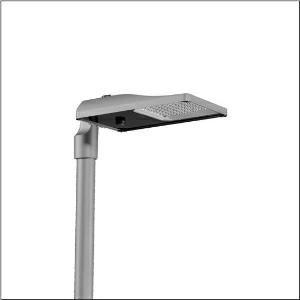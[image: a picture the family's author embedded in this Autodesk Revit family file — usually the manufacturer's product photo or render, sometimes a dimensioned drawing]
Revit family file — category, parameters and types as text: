
# Revit family: streetlight_sl_31_midi___st0_5a_5xh7b31t08ma_78a8
name_source: partatom
category: Lighting Fixtures
units: mm (PartAtom-declared; Revit-internal decimal feet)

## family parameters
Cut with Voids When Loaded = No
Host = Face
Light Source = No
Part Type = Normal
Room Calculation Point = No
Round Connector Dimension = Use Diameter
Shared = No

## types (1)
- --- (1 x LED, 19310 lm, 142.8 W, 3000K)
    Apparent Load = 143 VA
    CIE Flux Codes = 41 75 97 100 100
    Color Rendering = 70
    Color Temperature = 3000K
    Default Elevation = 1800 mm
    Description = Streetlight SL 31 midi, mast luminaire, primary light control with lens, of PMMA, primary optical cover: cover, of toughened safety glass, transparent, light distribution: ST0.5a, light emission: direct distribution, primary light characteristic: asymmetric, installation type: post-top, side-entry, LED, High Power LED, rated luminous flux: 19.310lm, luminous efficacy: 135lm/W, light colour: 730, colour temperature: 3000K, control: presetting dimming logarithmic, flexible luminous flux parameterisation, time-dependent luminous flux control, constant luminous flux control, power reduction, intelligent temperature release in ECG and LED module, overheat protection, with cable H07RN-F 2x 1.5mm², mains connection: 220..240V, AC, 50/60Hz, connection cable pre-assembled, cable length: 12,5m, start of lifetime: 143W, end of service life: 159W, reduction: 60W, luminaire housing, of diecast aluminium, powder-coated, Siteco® metallic grey (DB 702S), corrosivity category C5 high according to DIN EN ISO 12944, sealing non-destructively replaceable, multi-level sealing system, mast flange (76/60mm) included as standard, inclination: -15°..+20° (post-top) | -20°..+20° (side-entry), adjustable in 5° steps, no sealing on luminaire upper side, Smart Interface below and above, protection rating (complete): IP66, insulation class (complete): insulation class II (safety insulation), certification: CE, ENEC, ENEC+, VDE, UKCA, ZD4i, impact resistance: IK09, permissible operating ambient temperature for outdoor applications: -40..+50°C, standard-compliant lighting for roads and squares, packaging unit: 1 piece

Light Distribution: ST0.5a
    Height = 79 mm
    Lamp = 1 x LED
    Lamp Light Flux = 19310 lm
    Lamp Power = 142.8 W
    Lamp count = 1
    Length = 577 mm
    Luminous efficacy = 135 lm/W
    Manufacturer = Siteco
    ModVariant = No
    Model = 5XH7B31T08MA
    Number of Poles = 1
    OnlyDefault = Yes
    Power Factor = 1
    Product Name = Streetlight SL 31 midi | ST0.5a
    Product group = mast luminaire | pylon top
    ProductGroupID = 6100
    Protection Class = Protection class II
    Protection Degree = IP 66
    RLX_Detail_Level = 1
    RLX_Emergency_Light_Flux = 0 lm
    RLX_Emergency_Type = 0
    RLX_Emergency_Type_DB = No
    RlxData = <blob elided: 54245 chars, md5=f1b1f9f1>
    Socket = socket
    Standby Power = 0 W
    System Light Flux = 19309 lm
    System Power = 143 W
    Type Comments = factory setting: luminous flux: 100 % | dim-lin: 254 | 735 mA
    Type Image = l_1300321.jpg
    URL = http://relux.com
    VarID = @adj_016357
    Voltage = 0 V
    Weight = 0.00 kg
    Width = 362 mm

## geometry (parser evidence)
native form markers: Blend x4, Sweep x11
no freeform markers — native parametric forms only
